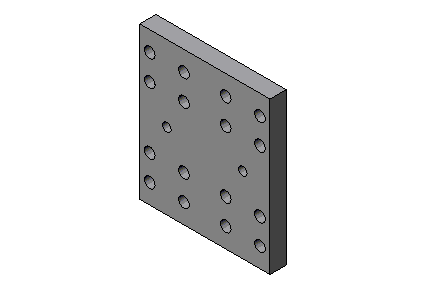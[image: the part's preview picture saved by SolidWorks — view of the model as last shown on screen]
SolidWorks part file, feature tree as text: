
SOLIDWORKS PART (.sldprt)
format: sldprt  version: not decoded by parser v0  size: 297,984 bytes
history: native  units: mm
features: sketch x5, hole x2, extrude x1 (+10 scaffold rows collapsed)
feature tree (18):
  scaffold x10  (default folders/planes/origin — collapsed)
  sketch  "Sketch1"  dims[D1=76.2mm D2=88.9mm]
  extrude  "Extrude1"  Depth=9.525mm
  hole  "CBORE for M3 SHCS1"  Diameter=3.5mm Depth=9.525mm
  sketch  "Sketch3"  dims[c1.D1=15.0mm c1.D2=20.0mm c1.D3=15.0mm c1.D4=20.0mm c1.D5=50.8mm c1.D6=20.0mm c2.D3=15.875mm]
  sketch  "Sketch2"  dims[hole-wizard template sketch: 41 standard entries collapsed; hole parameters kept: c12.Thru Hole Dia.=3.5mm c12.Thru Hole Depth=9.525mm c12.C'Bore Dia.=6.2mm c12.C'Bore Depth=6.0mm]
  hole  "CBORE for #10 Socket Head Cap Screw1"  Diameter=4.9784mm Depth=9.525mm
  sketch  "Sketch5"  dims[D1=44.45mm D2=50.8mm]
  sketch  "Sketch4"  dims[hole-wizard template sketch: 42 standard entries collapsed; hole parameters kept: c12.Thru Hole Depth=9.525mm c12.C'Bore Dia.=9.525mm c12.C'Bore Depth=4.826mm]
decode coverage: 8 of 8 modeling features carry decoded parameters
note: ~ marks probable driven/reference dimensions
note: suppression state not decoded; provenance and decode notes live in map.json
